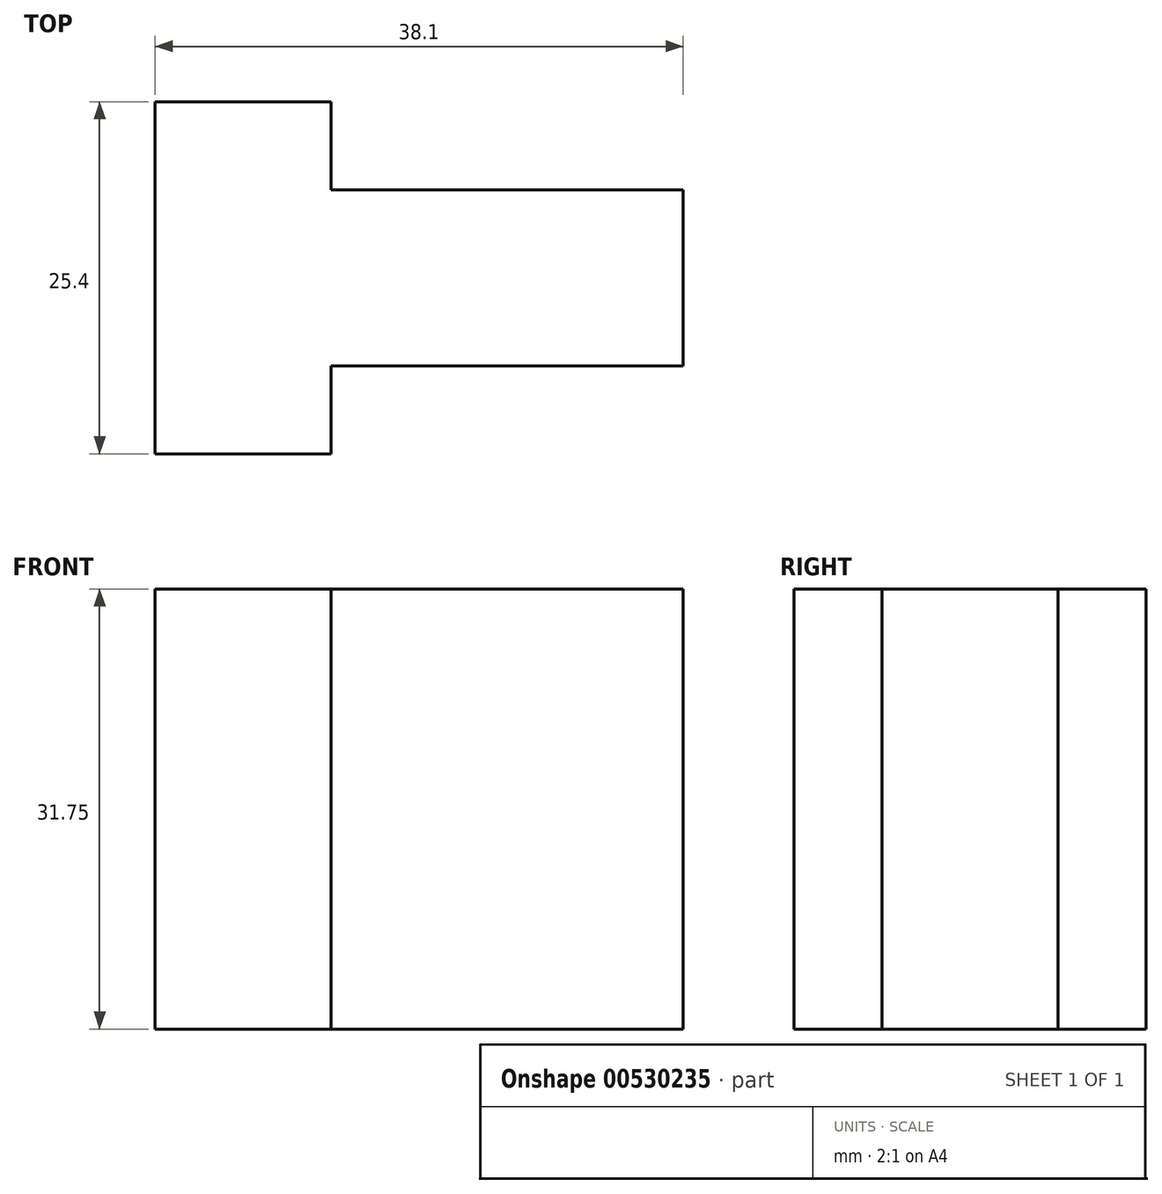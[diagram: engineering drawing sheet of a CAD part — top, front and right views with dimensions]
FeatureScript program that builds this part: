
annotation { "Feature Type Name" : "Feature", "Feature Type Description" : "" }
export const myFeature = defineFeature(function(context is Context, id is Id, definition is map)
    precondition{}
    {
        {
            var Q0;
            Q0=qCreatedBy(makeId("Top.planeOp"),FACE);
            var sketch = newSketch(context, id + "F0", { "sketchPlane" : qUnion([Q0])});
            skLineSegment(sketch, "E0", {"start": v(-50.11, 0) * mm, "end": v(-75.51, 0) * mm});
            skLineSegment(sketch, "E1", {"start": v(-75.51, 0) * mm, "end": v(-75.51, -6.35) * mm});
            skLineSegment(sketch, "E2", {"start": v(-75.51, -6.35) * mm, "end": v(-88.21, -6.35) * mm});
            skLineSegment(sketch, "E3", {"start": v(-88.21, -6.35) * mm, "end": v(-88.21, 19.05) * mm});
            skLineSegment(sketch, "E4", {"start": v(-88.21, 19.05) * mm, "end": v(-75.51, 19.05) * mm});
            skLineSegment(sketch, "E5", {"start": v(-75.51, 19.05) * mm, "end": v(-75.51, 12.7) * mm});
            skLineSegment(sketch, "E6", {"start": v(-75.51, 12.7) * mm, "end": v(-50.11, 12.7) * mm});
            skLineSegment(sketch, "E7", {"start": v(-50.11, 12.7) * mm, "end": v(-50.11, 0) * mm});
            skSolve(sketch);
        }
        {
            var Q0;
            Q0 = qSketchRegion(id + "F0", true);
            extrude(context, id + "F1", {"entities" : qUnion([Q0]), "depth" : 31.75 * mm, "offsetDistance" : 25.4 * mm});
        }
    });
